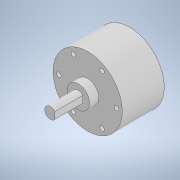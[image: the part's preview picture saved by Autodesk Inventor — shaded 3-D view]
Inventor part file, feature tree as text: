
AUTODESK INVENTOR PART (.ipt)
format: ipt  version: 2022 (Build 260153000, 153)  size: 133,632 bytes
history: native  units: mm
features: extrude x4, sketch x4, pattern_circular x1, projected_geometry x1
ambient origin geometry x8: Origin, YZ Plane, XZ Plane, XY Plane, X Axis, Y Axis, Z Axis, Center Point
bodies: Solid1 (feature_tree)
feature tree (10):
  extrude  "Extrusion1"  Depth=22.5mm TaperAngle=0.0deg
  extrude  "Extrusion2"  Depth=5.0mm TaperAngle=0.0deg
  extrude  "Extrusion3"  Depth=6.0mm
  extrude  "Extrusion4"  Depth=15.0mm
  pattern_circular  "Circular Pattern1"  [2 undecoded]
  sketch  "Sketch1"  dims[d0=37.0mm d1=22.5mm d2=0.0mm]
  sketch  "Sketch2"  dims[d3=12.0mm d4=5.0mm d5=0.0mm]
  sketch  "Sketch3"  dims[d6=6.0mm d7=5.4mm]
  sketch  "Sketch4"  dims[d8=15.0mm d9=0.0mm d10=30.83mm d11=2.4mm d12=15.0mm d13=0.0mm d14=30.0mm d15=360.0deg]
  projected_geometry  "Projected Loop1"
note: 2 required parameter values undecoded (feature->parameter linkage not recoverable at this tier; creation-order binding heuristic only, values carry confidence <= 0.55)
